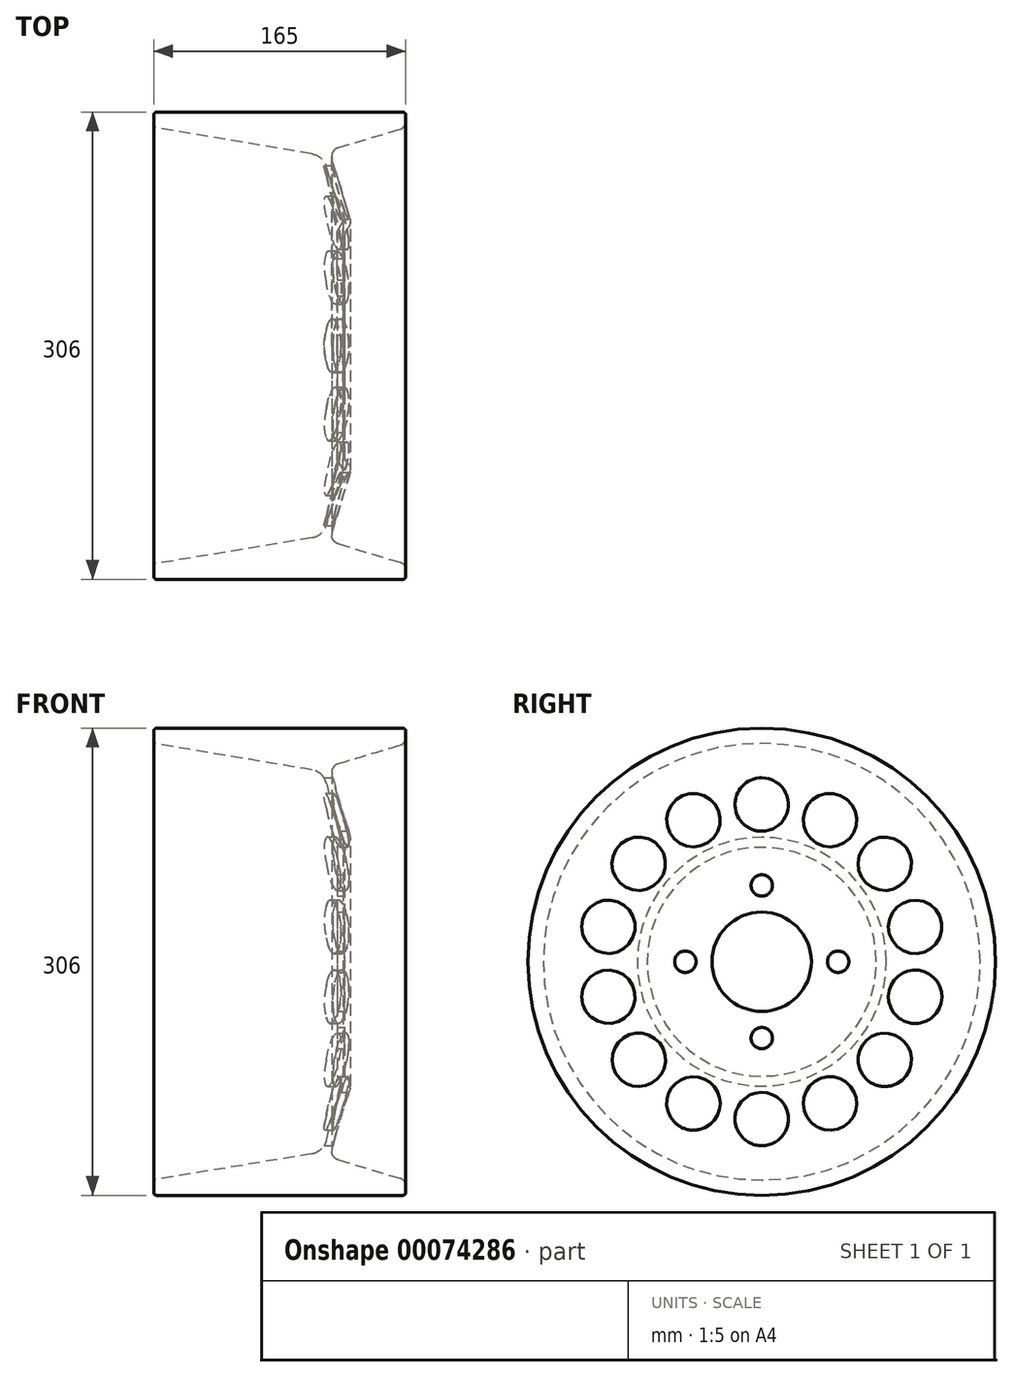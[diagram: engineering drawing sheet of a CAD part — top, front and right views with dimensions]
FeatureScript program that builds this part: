
annotation { "Feature Type Name" : "Feature", "Feature Type Description" : "" }
export const myFeature = defineFeature(function(context is Context, id is Id, definition is map)
    precondition{}
    {
        {
            var Q0;
            Q0=qCreatedBy(makeId("Front.planeOp"),FACE);
            var sketch = newSketch(context, id + "F0", { "sketchPlane" : qUnion([Q0])});
            skLineSegment(sketch, "E0", {"start": v(3.19, 0) * mm, "end": v(76.81, 0) * mm, "construction": true});
            skLineSegment(sketch, "E1", {"start": v(-37.97, 153) * mm, "end": v(121.37, 153) * mm, "construction": true});
            skLineSegment(sketch, "E2", {"start": v(0, 0) * mm, "end": v(0, 170.61) * mm, "construction": true});
            skLineSegment(sketch, "E3", {"start": v(-125, 0) * mm, "end": v(-125, 173.72) * mm, "construction": true});
            skLineSegment(sketch, "E4", {"start": v(40, 180.56) * mm, "end": v(40, 0) * mm, "construction": true});
            skPoint(sketch, "E4.startSnap0", {"position": v(40, 0) * mm});
            skLineSegment(sketch, "E5", {"start": v(96.33, 75) * mm, "end": v(-188.56, 75) * mm, "construction": true});
            skLineSegment(sketch, "E6", {"start": v(0, 0) * mm, "end": v(0, 72.39) * mm});
            skLineSegment(sketch, "E7", {"start": v(-5, 0) * mm, "end": v(-5, 75) * mm});
            skLineSegment(sketch, "E8", {"start": v(40, 153) * mm, "end": v(-125, 153) * mm});
            skPoint(sketch, "E9.orphan", {"position": v(41.7, 153) * mm});
            skLineSegment(sketch, "E10", {"start": v(40, 153) * mm, "end": v(40, 143) * mm});
            skLineSegment(sketch, "E11", {"start": v(40, 143) * mm, "end": v(-4.25, 129.73) * mm});
            skLineSegment(sketch, "E12", {"start": v(-8.27, 122.25) * mm, "end": v(3.59, 82.93) * mm});
            skLineSegment(sketch, "E13", {"start": v(1.94, 76.8) * mm, "end": v(1.9, 76.78) * mm});
            skPoint(sketch, "E14.visualSharp", {"position": v(4.67, 79.35) * mm});
            skArc(sketch, "E14.filletArc", {"start": v(1.94, 76.8) * mm, "mid": v(3.64, 79.63) * mm, "end": v(3.59, 82.93) * mm});
            skPoint(sketch, "E15.visualSharp", {"position": v(-10, 128) * mm});
            skArc(sketch, "E15.filletArc", {"start": v(-4.25, 129.73) * mm, "mid": v(-7.8, 126.82) * mm, "end": v(-8.27, 122.25) * mm});
            skLineSegment(sketch, "E16", {"start": v(-125, 153) * mm, "end": v(-125, 143) * mm});
            skLineSegment(sketch, "E17.1", {"start": v(-12.01, 117.35) * mm, "end": v(-1.2, 81.48) * mm});
            skLineSegment(sketch, "E18", {"start": v(-1.2, 81.48) * mm, "end": v(-5, 75) * mm});
            skLineSegment(sketch, "E19", {"start": v(-125, 143) * mm, "end": v(-21.52, 125.72) * mm});
            skPoint(sketch, "E20.visualSharp", {"position": v(-14.17, 124.5) * mm});
            skArc(sketch, "E20.filletArc", {"start": v(-12.01, 117.35) * mm, "mid": v(-15.57, 122.9) * mm, "end": v(-21.52, 125.72) * mm});
            skLineSegment(sketch, "E21", {"start": v(-5, 0) * mm, "end": v(0, 0) * mm});
            skPoint(sketch, "E22.visualSharp", {"position": v(0, 75) * mm});
            skArc(sketch, "E22.filletArc", {"start": v(1.9, 76.78) * mm, "mid": v(0.5, 74.78) * mm, "end": v(0, 72.39) * mm});
            skSolve(sketch);
        }
        {
            var Q0;
            Q0 = qSketchRegion(id + "F0", true);
            var Q1;
            Q1=sQuery(id+"F0.wireOp",EDGE,"E0");
            revolve(context, id + "F1", {"entities" : qUnion([Q0]), "axis" : qUnion([Q1]), "revolveType" : RevolveType.FULL});
        }
        {
            var Q0;
            Q0=makeQuery(id+"F1.opRevolve","SWEPT_FACE",FACE,{"disambiguationData":[OSD([sQuery(id+"F0.wireOp",EDGE,"E6")])]});
            var sketch = newSketch(context, id + "F2", { "sketchPlane" : qUnion([Q0])});
            skCircle(sketch, "E23", {"center": v(0, 0) * mm, "radius": 32.5 * mm});
            skSolve(sketch);
        }
        {
            var Q0;
            Q0 = qSketchRegion(id + "F2", true);
            extrude(context, id + "F3", {"entities" : qUnion([Q0]), "operationType" : NewBodyOperationType.REMOVE, "oppositeDirection" : true, "depth" : 25 * mm});
        }
        {
            var Q0;
            Q0=makeQuery(id+"F1.opRevolve","SWEPT_FACE",FACE,{"disambiguationData":[OSD([sQuery(id+"F0.wireOp",EDGE,"E6")])]});
            var sketch = newSketch(context, id + "F4", { "sketchPlane" : qUnion([Q0])});
            skCircle(sketch, "E24", {"center": v(0, 50) * mm, "radius": 7 * mm});
            skCircle(sketch, "E25.1.0", {"center": v(-50, 0) * mm, "radius": 7 * mm});
            skCircle(sketch, "E25.2.0", {"center": v(0, -50) * mm, "radius": 7 * mm});
            skCircle(sketch, "E25.3.0", {"center": v(50, 0) * mm, "radius": 7 * mm});
            skPoint(sketch, "E25.center", {"position": v(0, 0) * mm});
            skSolve(sketch);
        }
        {
            var Q0;
            Q0 = qSketchRegion(id + "F4", true);
            extrude(context, id + "F5", {"entities" : qUnion([Q0]), "operationType" : NewBodyOperationType.REMOVE, "oppositeDirection" : true, "depth" : 25 * mm});
        }
        {
            var Q0;
            Q0=makeQuery(id+"F1.opRevolve","SWEPT_FACE",FACE,{"disambiguationData":[OSD([sQuery(id+"F0.wireOp",EDGE,"E10")])]});
            var sketch = newSketch(context, id + "F6", { "sketchPlane" : qUnion([Q0])});
            skCircle(sketch, "E26", {"center": v(0, 103) * mm, "radius": 17.5 * mm});
            skCircle(sketch, "E27.1.0", {"center": v(-44.7, 92.8) * mm, "radius": 17.5 * mm});
            skCircle(sketch, "E27.2.0", {"center": v(-80.53, 64.22) * mm, "radius": 17.5 * mm});
            skCircle(sketch, "E27.3.0", {"center": v(-100.42, 22.92) * mm, "radius": 17.5 * mm});
            skCircle(sketch, "E27.4.0", {"center": v(-100.42, -22.92) * mm, "radius": 17.5 * mm});
            skCircle(sketch, "E27.5.0", {"center": v(-80.53, -64.22) * mm, "radius": 17.5 * mm});
            skCircle(sketch, "E27.6.0", {"center": v(-44.7, -92.8) * mm, "radius": 17.5 * mm});
            skCircle(sketch, "E27.7.0", {"center": v(0, -103) * mm, "radius": 17.5 * mm});
            skCircle(sketch, "E27.8.0", {"center": v(44.7, -92.8) * mm, "radius": 17.5 * mm});
            skCircle(sketch, "E27.9.0", {"center": v(80.53, -64.22) * mm, "radius": 17.5 * mm});
            skCircle(sketch, "E27.10.0", {"center": v(100.42, -22.92) * mm, "radius": 17.5 * mm});
            skCircle(sketch, "E27.11.0", {"center": v(100.42, 22.92) * mm, "radius": 17.5 * mm});
            skCircle(sketch, "E27.12.0", {"center": v(80.53, 64.22) * mm, "radius": 17.5 * mm});
            skCircle(sketch, "E27.13.0", {"center": v(44.7, 92.8) * mm, "radius": 17.5 * mm});
            skPoint(sketch, "E27.center", {"position": v(0, 0) * mm});
            skSolve(sketch);
        }
        {
            var Q0;
            Q0 = qSketchRegion(id + "F6", true);
            extrude(context, id + "F7", {"entities" : qUnion([Q0]), "operationType" : NewBodyOperationType.REMOVE, "oppositeDirection" : true, "depth" : 100 * mm});
        }
        {
            var Q0;
            Q0=makeQuery(id+"F1.opRevolve","SWEPT_EDGE",EDGE,{"disambiguationData":[OSD([sQuery(id+"F0.wireOp",EDGE,"E10"),sQuery(id+"F0.wireOp",EDGE,"E11")])]});
            fillet(context, id + "F8", {"entities" : qUnion([Q0]), "radius" : 5 * mm, "tangentPropagation" : true, "allowEdgeOverflow" : false});
        }
        {
            var Q0;
            Q0=makeQuery(id+"F1.opRevolve","SWEPT_EDGE",EDGE,{"disambiguationData":[OSD([sQuery(id+"F0.wireOp",EDGE,"E8"),sQuery(id+"F0.wireOp",EDGE,"E10")])]});
            fillet(context, id + "F9", {"entities" : qUnion([Q0]), "radius" : 2 * mm, "tangentPropagation" : true, "allowEdgeOverflow" : false});
        }
        {
            var Q0;
            Q0=makeQuery(id+"F1.opRevolve","SWEPT_EDGE",EDGE,{"disambiguationData":[OSD([sQuery(id+"F0.wireOp",EDGE,"E8"),sQuery(id+"F0.wireOp",EDGE,"E16")])]});
            fillet(context, id + "F10", {"entities" : qUnion([Q0]), "radius" : 2 * mm, "tangentPropagation" : true, "allowEdgeOverflow" : false});
        }
    });
